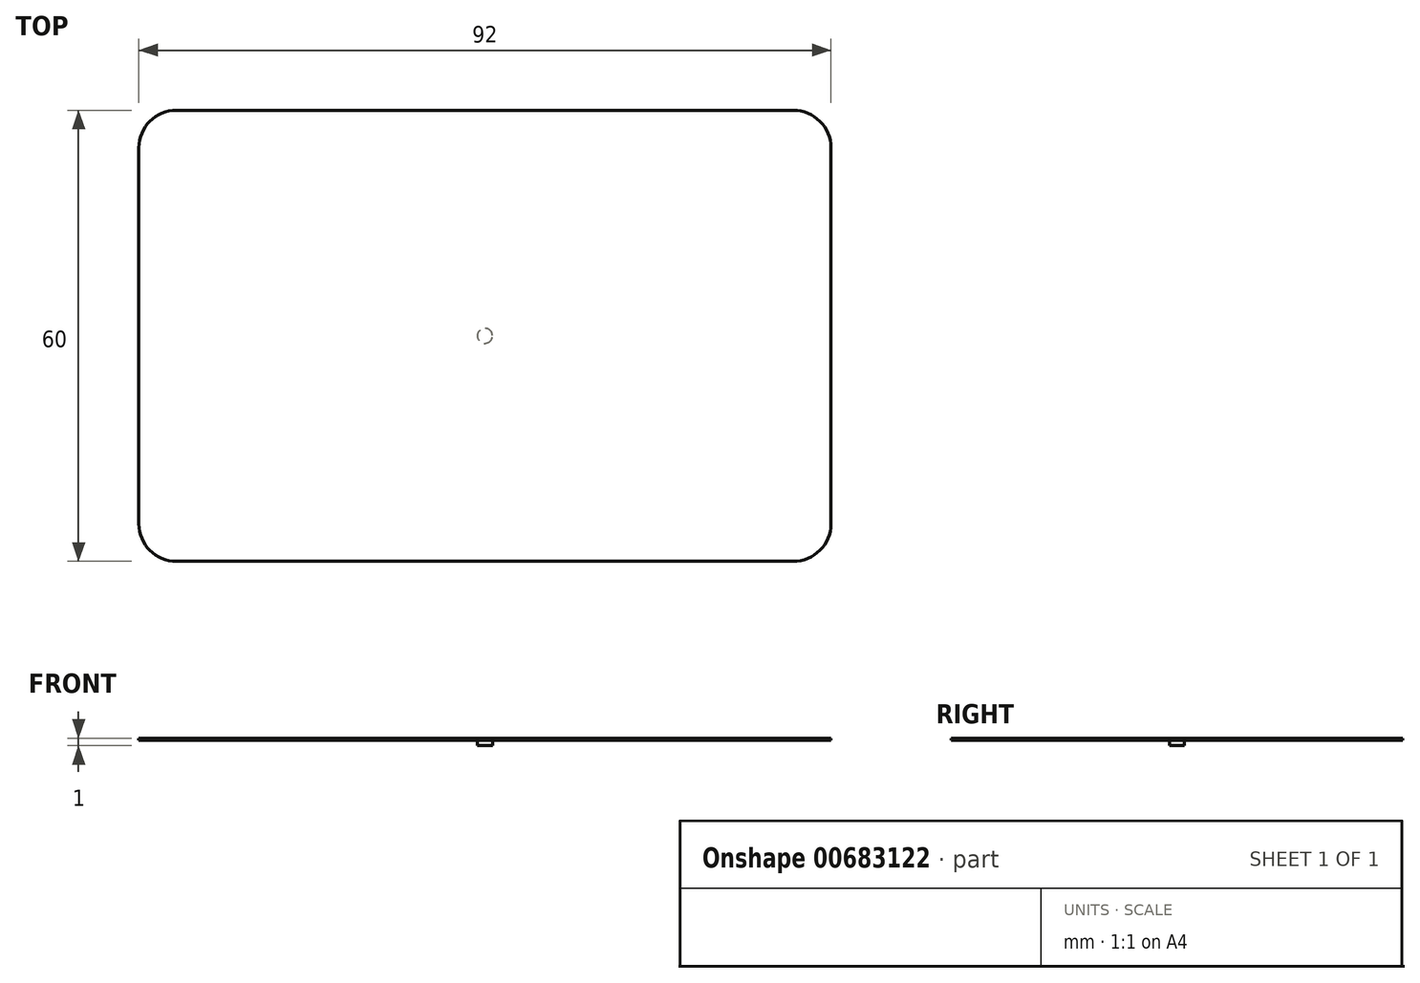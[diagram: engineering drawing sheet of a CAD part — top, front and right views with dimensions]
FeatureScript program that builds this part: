
annotation { "Feature Type Name" : "Feature", "Feature Type Description" : "" }
export const myFeature = defineFeature(function(context is Context, id is Id, definition is map)
    precondition{}
    {
        {
            var Q0;
            Q0=qCreatedBy(makeId("Top.planeOp"),FACE);
            var sketch = newSketch(context, id + "F0", { "sketchPlane" : qUnion([Q0])});
            skLineSegment(sketch, "E0.bottom", {"start": v(46, 30) * mm, "end": v(-46, 30) * mm});
            skLineSegment(sketch, "E0.top", {"start": v(46, -30) * mm, "end": v(-46, -30) * mm});
            skLineSegment(sketch, "E0.left", {"start": v(46, 30) * mm, "end": v(46, -30) * mm});
            skLineSegment(sketch, "E0.right", {"start": v(-46, 30) * mm, "end": v(-46, -30) * mm});
            skPoint(sketch, "E0.middle", {"position": v(0, 0) * mm});
            skSolve(sketch);
        }
        {
            var Q0;
            Q0=makeQuery(id+"F0.imprint","IMPRINT",FACE,{"disambiguationData":[TD([[makeQuery(id+"F0.imprint","IMPRINT",EDGE,{"derivedFrom":sQuery(id+"F0.wireOp",EDGE,"E0.bottom")}),1.0]])]});
            extrude(context, id + "F1", {"entities" : qUnion([Q0]), "depth" : .3 * mm, "offsetDistance" : 25 * mm});
        }
        {
            var Q0;
            Q0=makeQuery(id+"F1.opExtrude","SWEPT_EDGE",EDGE,{"disambiguationData":[OSD([sQuery(id+"F0.wireOp",EDGE,"E0.bottom"),sQuery(id+"F0.wireOp",EDGE,"E0.right")])]});
            var Q1;
            Q1=makeQuery(id+"F1.opExtrude","SWEPT_EDGE",EDGE,{"disambiguationData":[OSD([sQuery(id+"F0.wireOp",EDGE,"E0.top"),sQuery(id+"F0.wireOp",EDGE,"E0.right")])]});
            var Q2;
            Q2=makeQuery(id+"F1.opExtrude","SWEPT_EDGE",EDGE,{"disambiguationData":[OSD([sQuery(id+"F0.wireOp",EDGE,"E0.bottom"),sQuery(id+"F0.wireOp",EDGE,"E0.left")])]});
            var Q3;
            Q3=makeQuery(id+"F1.opExtrude","SWEPT_EDGE",EDGE,{"disambiguationData":[OSD([sQuery(id+"F0.wireOp",EDGE,"E0.top"),sQuery(id+"F0.wireOp",EDGE,"E0.left")])]});
            fillet(context, id + "F2", {"entities" : qUnion([Q0, Q1, Q2, Q3]), "radius" : 5 * mm, "tangentPropagation" : true, "allowEdgeOverflow" : false});
        }
        {
            var Q0;
            Q0=makeQuery(id+"F1.opExtrude","CAP_FACE",FACE,{"disambiguationData":[OSD([sQuery(id+"F0.wireOp",EDGE,"E0.bottom"),sQuery(id+"F0.wireOp",EDGE,"E0.top"),sQuery(id+"F0.wireOp",EDGE,"E0.left"),sQuery(id+"F0.wireOp",EDGE,"E0.right")])],"isStart":true});
            var sketch = newSketch(context, id + "F3", { "sketchPlane" : qUnion([Q0])});
            skCircle(sketch, "E1", {"center": v(0, 0) * mm, "radius": 1 * mm});
            skSolve(sketch);
        }
        {
            var Q0;
            Q0=makeQuery(id+"F3.imprint","IMPRINT",FACE,{"disambiguationData":[TD([[makeQuery(id+"F3.imprint","IMPRINT",EDGE,{"derivedFrom":sQuery(id+"F3.wireOp",EDGE,"E1")}),1.0]])]});
            extrude(context, id + "F4", {"entities" : qUnion([Q0]), "operationType" : NewBodyOperationType.ADD, "depth" : .7 * mm, "offsetDistance" : 25 * mm});
        }
    });
